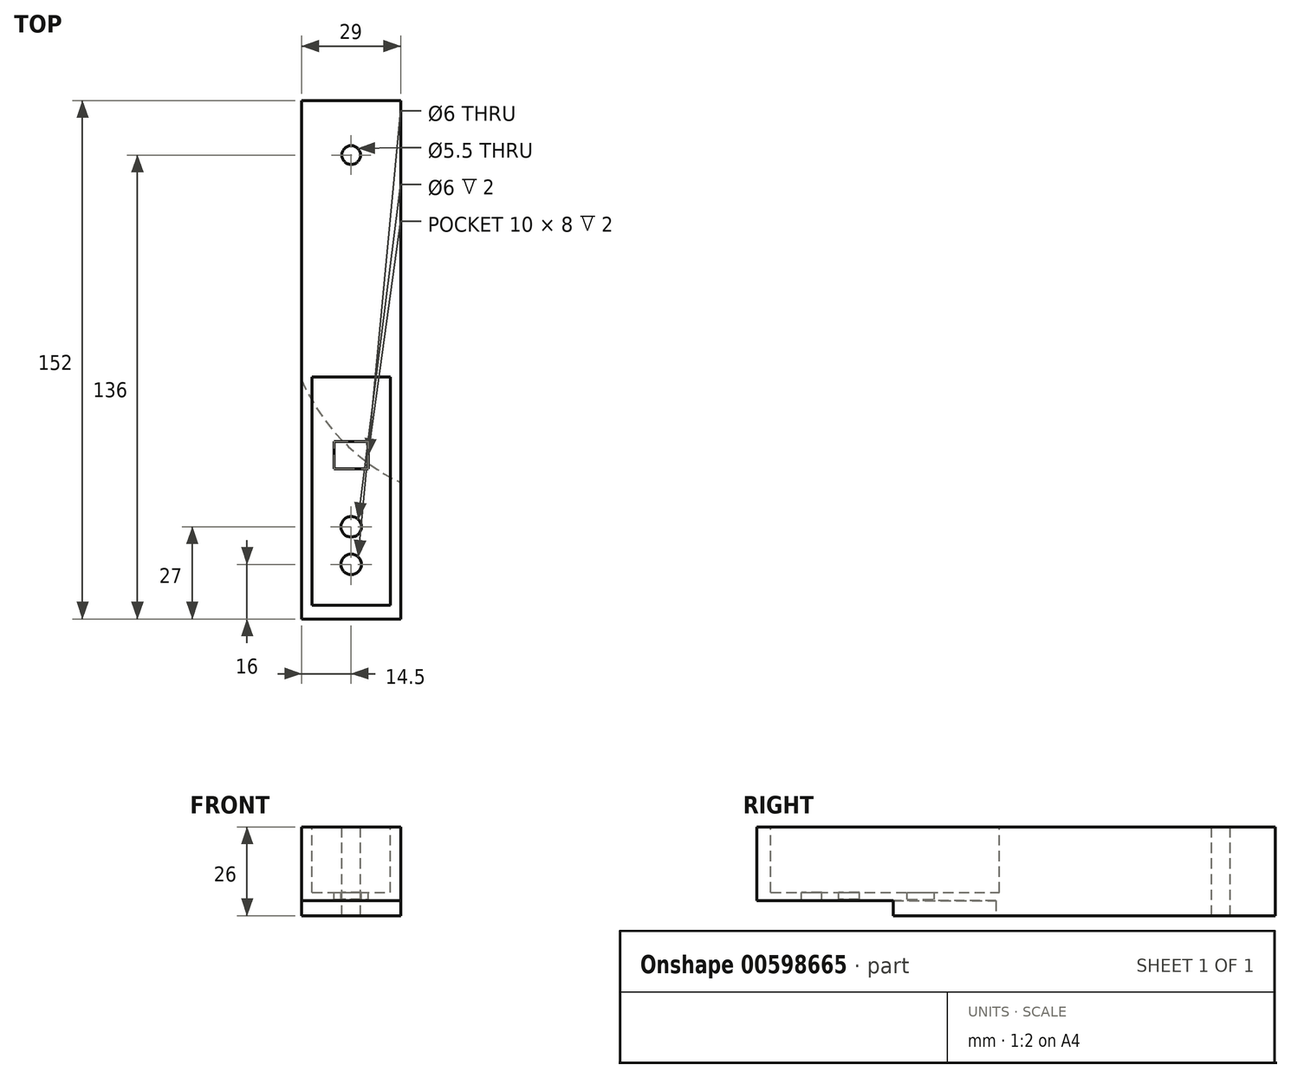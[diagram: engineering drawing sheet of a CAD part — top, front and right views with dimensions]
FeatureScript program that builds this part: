
annotation { "Feature Type Name" : "Feature", "Feature Type Description" : "" }
export const myFeature = defineFeature(function(context is Context, id is Id, definition is map)
    precondition{}
    {
        {
            var Q0;
            Q0=qCreatedBy(makeId("Top.planeOp"),FACE);
            var sketch = newSketch(context, id + "F0", { "sketchPlane" : qUnion([Q0])});
            skLineSegment(sketch, "E0.bottom", {"start": v(-14.5, 76) * mm, "end": v(14.5, 76) * mm});
            skLineSegment(sketch, "E0.top", {"start": v(-14.5, -76) * mm, "end": v(14.5, -76) * mm});
            skLineSegment(sketch, "E0.left", {"start": v(-14.5, 76) * mm, "end": v(-14.5, -76) * mm});
            skLineSegment(sketch, "E0.right", {"start": v(14.5, 76) * mm, "end": v(14.5, -76) * mm});
            skSolve(sketch);
        }
        {
            var Q0;
            Q0=makeQuery(id+"F0.imprint","IMPRINT",FACE,{"disambiguationData":[TD([[makeQuery(id+"F0.imprint","IMPRINT",EDGE,{"derivedFrom":sQuery(id+"F0.wireOp",EDGE,"E0.bottom")}),-1.0]])]});
            extrude(context, id + "F1", {"entities" : qUnion([Q0]), "depth" : 26 * mm, "offsetDistance" : 25 * mm});
        }
        {
            var Q0;
            Q0=makeQuery(id+"F1.opExtrude","CAP_FACE",FACE,{"disambiguationData":[OSD([sQuery(id+"F0.wireOp",EDGE,"E0.bottom"),sQuery(id+"F0.wireOp",EDGE,"E0.top"),sQuery(id+"F0.wireOp",EDGE,"E0.left"),sQuery(id+"F0.wireOp",EDGE,"E0.right")])],"isStart":false});
            var sketch = newSketch(context, id + "F2", { "sketchPlane" : qUnion([Q0])});
            skCircle(sketch, "E1", {"center": v(0, -60) * mm, "radius": 3 * mm});
            skCircle(sketch, "E2", {"center": v(0, 60) * mm, "radius": 2.75 * mm});
            skSolve(sketch);
        }
        {
            var Q0;
            Q0=makeQuery(id+"F2.imprint","IMPRINT",FACE,{"disambiguationData":[TD([[makeQuery(id+"F2.imprint","IMPRINT",EDGE,{"derivedFrom":sQuery(id+"F2.wireOp",EDGE,"E1")}),1.0]])]});
            var Q1;
            Q1=makeQuery(id+"F2.imprint","IMPRINT",FACE,{"disambiguationData":[TD([[makeQuery(id+"F2.imprint","IMPRINT",EDGE,{"derivedFrom":sQuery(id+"F2.wireOp",EDGE,"E2")}),1.0]])]});
            var Q2;
            Q2=sQuery(id+"F2.wireOp",EDGE,"E2");
            var Q3;
            Q3=sQuery(id+"F2.wireOp",EDGE,"E1");
            extrude(context, id + "F3", {"entities" : qUnion([Q0, Q1]), "operationType" : NewBodyOperationType.REMOVE, "surfaceEntities" : qUnion([Q2, Q3]), "endBound" : BoundingType.THROUGH_ALL, "oppositeDirection" : true, "depth" : 25 * mm, "offsetDistance" : 25 * mm});
        }
        {
            var Q0;
            Q0=makeQuery(id+"F1.opExtrude","CAP_FACE",FACE,{"disambiguationData":[OSD([sQuery(id+"F0.wireOp",EDGE,"E0.bottom"),sQuery(id+"F0.wireOp",EDGE,"E0.top"),sQuery(id+"F0.wireOp",EDGE,"E0.left"),sQuery(id+"F0.wireOp",EDGE,"E0.right")])],"isStart":false});
            var sketch = newSketch(context, id + "F4", { "sketchPlane" : qUnion([Q0])});
            skLineSegment(sketch, "E3.bottom", {"start": v(-11.5, -72) * mm, "end": v(11.5, -72) * mm});
            skLineSegment(sketch, "E3.top", {"start": v(-11.5, -5) * mm, "end": v(11.5, -5) * mm});
            skLineSegment(sketch, "E3.left", {"start": v(-11.5, -72) * mm, "end": v(-11.5, -5) * mm});
            skLineSegment(sketch, "E3.right", {"start": v(11.5, -72) * mm, "end": v(11.5, -5) * mm});
            skCircle(sketch, "E4.0", {"center": v(0, -60) * mm, "radius": 3 * mm});
            skSolve(sketch);
        }
        {
            var Q0;
            Q0=makeQuery(id+"F4.imprint","IMPRINT",FACE,{"disambiguationData":[TD([[makeQuery(id+"F4.imprint","IMPRINT",EDGE,{"derivedFrom":sQuery(id+"F4.wireOp",EDGE,"E3.bottom")}),1.0]])]});
            extrude(context, id + "F5", {"entities" : qUnion([Q0]), "operationType" : NewBodyOperationType.REMOVE, "oppositeDirection" : true, "depth" : 19.2 * mm, "offsetDistance" : 25 * mm});
        }
        {
            var Q0;
            Q0=makeQuery(id+"F5.boolean.opBoolean","COPY",FACE,{"derivedFrom":makeQuery(id+"F5.opExtrude","CAP_FACE",FACE,{"disambiguationData":[OSD([sQuery(id+"F4.wireOp",EDGE,"E3.bottom"),sQuery(id+"F4.wireOp",EDGE,"E3.top"),sQuery(id+"F4.wireOp",EDGE,"E3.left"),sQuery(id+"F4.wireOp",EDGE,"E3.right"),sQuery(id+"F4.wireOp",EDGE,"E4.0")])],"isStart":false})});
            var sketch = newSketch(context, id + "F6", { "sketchPlane" : qUnion([Q0])});
            skCircle(sketch, "E5.0", {"center": v(0, -60) * mm, "radius": 3 * mm});
            skCircle(sketch, "E6", {"center": v(0, -49) * mm, "radius": 3 * mm});
            skLineSegment(sketch, "E7.bottom", {"start": v(-5, -32) * mm, "end": v(5, -32) * mm});
            skLineSegment(sketch, "E7.top", {"start": v(-5, -24) * mm, "end": v(5, -24) * mm});
            skLineSegment(sketch, "E7.left", {"start": v(-5, -32) * mm, "end": v(-5, -24) * mm});
            skLineSegment(sketch, "E7.right", {"start": v(5, -32) * mm, "end": v(5, -24) * mm});
            skSolve(sketch);
        }
        {
            var Q0;
            Q0=makeQuery(id+"F6.imprint","IMPRINT",FACE,{"disambiguationData":[TD([[makeQuery(id+"F6.imprint","IMPRINT",EDGE,{"derivedFrom":sQuery(id+"F6.wireOp",EDGE,"E7.bottom")}),1.0]])]});
            var Q1;
            Q1=makeQuery(id+"F6.imprint","IMPRINT",FACE,{"disambiguationData":[TD([[makeQuery(id+"F6.imprint","IMPRINT",EDGE,{"derivedFrom":sQuery(id+"F6.wireOp",EDGE,"E6")}),1.0]])]});
            extrude(context, id + "F7", {"entities" : qUnion([Q0, Q1]), "operationType" : NewBodyOperationType.REMOVE, "oppositeDirection" : true, "depth" : 2 * mm, "offsetDistance" : 25 * mm});
        }
        {
            var Q0;
            Q0=makeQuery(id+"F1.opExtrude","CAP_FACE",FACE,{"disambiguationData":[OSD([sQuery(id+"F0.wireOp",EDGE,"E0.bottom"),sQuery(id+"F0.wireOp",EDGE,"E0.top"),sQuery(id+"F0.wireOp",EDGE,"E0.left"),sQuery(id+"F0.wireOp",EDGE,"E0.right")])],"isStart":true});
            var sketch = newSketch(context, id + "F8", { "sketchPlane" : qUnion([Q0])});
            skLineSegment(sketch, "E8.bottom", {"start": v(14.5, 76) * mm, "end": v(-14.5, 76) * mm});
            skLineSegment(sketch, "E8.top", {"start": v(14.5, 36) * mm, "end": v(-14.5, 36) * mm});
            skLineSegment(sketch, "E8.left", {"start": v(14.5, 76) * mm, "end": v(14.5, 36) * mm});
            skLineSegment(sketch, "E8.right", {"start": v(-14.5, 76) * mm, "end": v(-14.5, 36) * mm});
            skArc(sketch, "E9", {"start": v(14.5, 36) * mm, "mid": v(-2.7, 23.6) * mm, "end": v(-14.5, 6) * mm});
            skSolve(sketch);
        }
        {
            var Q0;
            Q0=makeQuery(id+"F8.imprint","IMPRINT",FACE,{"disambiguationData":[TD([[makeQuery(id+"F8.imprint","IMPRINT",EDGE,{"derivedFrom":sQuery(id+"F8.wireOp",EDGE,"E8.bottom")}),-1.0]])]});
            var Q1;
            {var subQ0=sQuery(id+"F8.wireOp",EDGE,"E8.top");Q1=makeQuery(id+"F8.imprint","IMPRINT",FACE,{"disambiguationData":[TD([[makeQuery(id+"F8.imprint","IMPRINT",EDGE,{"derivedFrom":subQ0}),1.0]])]});}
            extrude(context, id + "F9", {"entities" : qUnion([Q0, Q1]), "operationType" : NewBodyOperationType.REMOVE, "oppositeDirection" : true, "depth" : 4.4 * mm, "offsetDistance" : 25 * mm});
        }
    });
